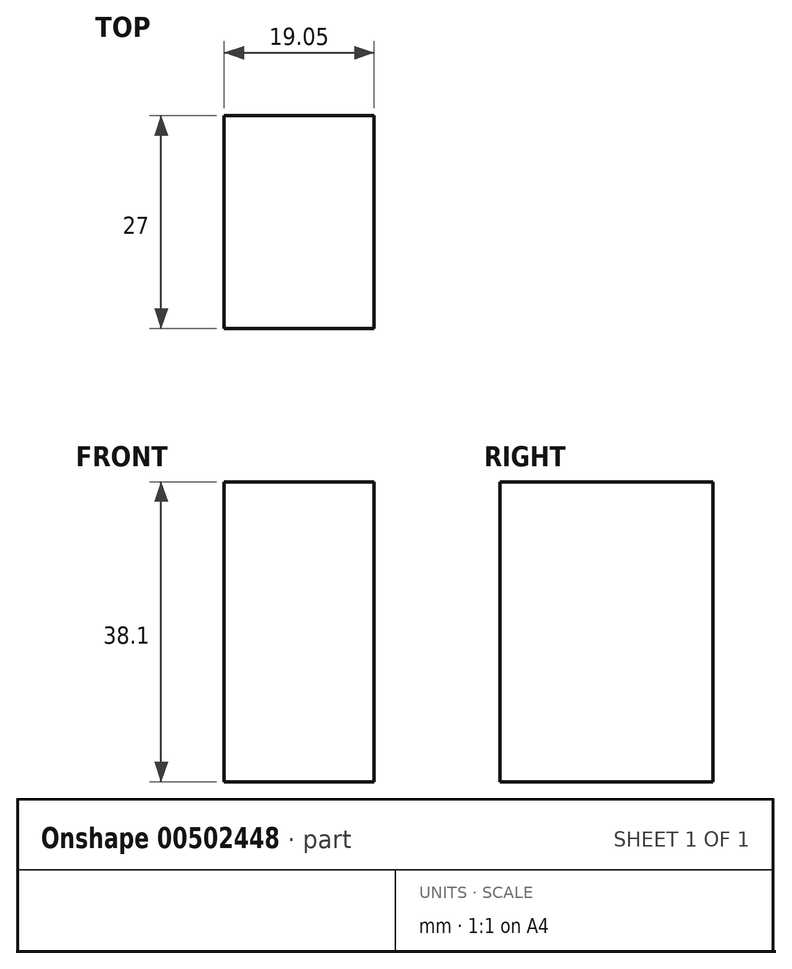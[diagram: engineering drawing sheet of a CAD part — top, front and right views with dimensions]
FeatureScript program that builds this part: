
annotation { "Feature Type Name" : "Feature", "Feature Type Description" : "" }
export const myFeature = defineFeature(function(context is Context, id is Id, definition is map)
    precondition{}
    {
        {
            assignVariable(context, id + "F0", {"name" : "BaseSide", "anyValue" : 27});
        }
        {
            var Q0;
            Q0=qCreatedBy(makeId("Front.planeOp"),FACE);
            var sketch = newSketch(context, id + "F1", { "sketchPlane" : qUnion([Q0])});
            skLineSegment(sketch, "E0.bottom", {"start": v(0, 38.1) * mm, "end": v(19.05, 38.1) * mm});
            skLineSegment(sketch, "E0.top", {"start": v(0, 0) * mm, "end": v(19.05, 0) * mm});
            skLineSegment(sketch, "E0.left", {"start": v(0, 38.1) * mm, "end": v(0, 0) * mm});
            skLineSegment(sketch, "E0.right", {"start": v(19.05, 38.1) * mm, "end": v(19.05, 0) * mm});
            skSolve(sketch);
        }
        {
            var Q0;
            Q0=makeQuery(id+"F1.imprint","IMPRINT",FACE,{"disambiguationData":[TD([[makeQuery(id+"F1.imprint","IMPRINT",EDGE,{"derivedFrom":sQuery(id+"F1.wireOp",EDGE,"E0.bottom")}),-1.0]])]});
            extrude(context, id + "F2", {"entities" : qUnion([Q0]), "depth" : (getVariable(context, 'BaseSide')) * mm});
        }
    });
